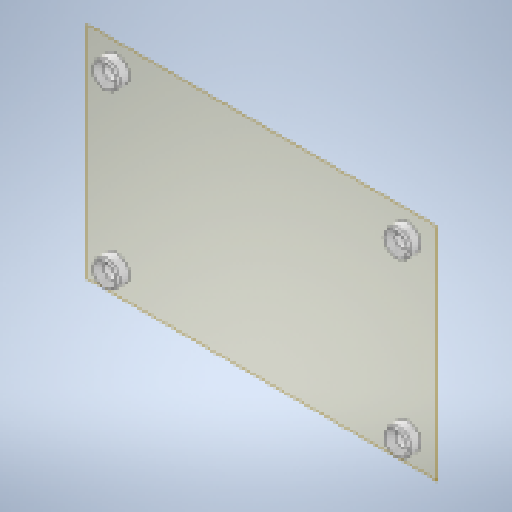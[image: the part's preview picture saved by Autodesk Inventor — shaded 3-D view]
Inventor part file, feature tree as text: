
AUTODESK INVENTOR PART (.ipt)
format: ipt  version: 2024.1 (Build 281209000, 209)  size: 163,328 bytes
history: native  units: mm
features: reference x4, other x3, plane x1, extrude x1, chamfer x1, fillet x1, sketch x1
ambient origin geometry x8: Origin, YZ Plane, XZ Plane, XY Plane, X Axis, Y Axis, Z Axis, Center Point
bodies: Body1 (feature_tree)
feature tree (12):
  other  "screw-shafts"
  plane  "Work Plane1"
  extrude  "Extrusion1"  Depth=1.0mm TaperAngle=0.0deg
  chamfer  "Chamfer1"  Distance=1.5mm Angle=45.0deg
  fillet  "Fillet1"  Radius=1.0mm
  sketch  "Sketch1"  dims[d0=7.0mm d1=3.25mm d2=0.0mm d3=1.5mm d4=2.0mm d5=45.0deg d6=1.0mm]
  reference  "Reference1"
  reference  "Reference2"
  reference  "Reference3"
  reference  "Reference4"
  other  "Assembly1"
  other  "diode-ladder-filter-synth-module:1"
